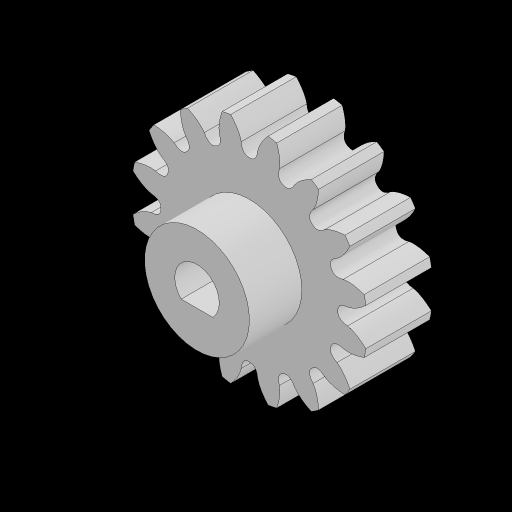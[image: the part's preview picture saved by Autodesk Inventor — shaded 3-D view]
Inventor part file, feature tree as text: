
AUTODESK INVENTOR PART (.ipt)
format: ipt  version: 2023.2 (Build 272271030, 271C)  size: 336,896 bytes
history: native  units: mm
features: extrude x4, sketch x3, pattern_circular x1, projected_geometry x1
ambient origin geometry x8: Origin, YZ Plane, XZ Plane, XY Plane, X Axis, Y Axis, Z Axis, Center Point
bodies: Solid1 (feature_tree)
feature tree (9):
  sketch  "Sketch1"  dims[d0=5.0mm d1=0.0mm d2=0.0mm d3=0.0mm]
  extrude  "Extrusion1"  TaperAngle=0.0deg  [1 undecoded]
  extrude  "Extrusion2"  Depth=3.0mm
  pattern_circular  "Circular Pattern1"  [2 undecoded]
  extrude  "Extrusion3"  TaperAngle=0.0deg  [1 undecoded]
  extrude  "Extrusion4"  Depth=4.0mm
  sketch  "Sketch2"  dims[d4=160.0mm d5=360.0deg d7=3.0mm]
  sketch  "Sketch3"  dims[d8=2.5mm d9=0.2mm d10=0.0mm d11=0.0mm d12=8.0mm d13=4.0mm d14=0.0mm]
  projected_geometry  "Projected Loop1"
note: 4 required parameter values undecoded (feature->parameter linkage not recoverable at this tier; creation-order binding heuristic only, values carry confidence <= 0.55)
